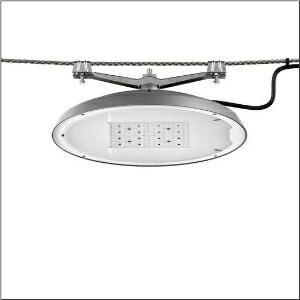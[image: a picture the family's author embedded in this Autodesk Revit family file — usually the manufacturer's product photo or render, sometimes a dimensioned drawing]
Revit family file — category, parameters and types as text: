
# Revit family: dl_r__50_iq_mini___st0_8s_5xa248v31f08me_3f47
name_source: partatom
category: Lighting Fixtures
units: mm (PartAtom-declared; Revit-internal decimal feet)

## family parameters
Cut with Voids When Loaded = No
Host = Face
Light Source = No
Part Type = Normal
Room Calculation Point = No
Round Connector Dimension = Use Diameter
Shared = No

## types (1)
- --- (1 x LED, 15660 lm, 107.8 W, 3000K)
    Apparent Load = 108 VA
    CIE Flux Codes = 38 75 97 100 100
    Color Rendering = 70
    Color Temperature = 3000K
    Default Elevation = 1800 mm
    Description = DL® 50 iQ mini, catenary luminaire, primary light control with lens, of PMMA, primary optical cover: cover, of toughened safety glass, transparent, light distribution: ST0.8s, light emission: direct distribution, primary light characteristic: symmetric, installation type: suspended mounting, LED, High Power LED, rated luminous flux: 15.660lm, luminous efficacy: 145lm/W, light colour: 730, colour temperature: 3000K, control gear: iQ Street-Remote, control: optimised constant luminous flux control (CLO 2.0), Desk-Remote (wireless, voltage-free reading and setting of iQ features in the workshop via application-optimized NFC function/RFID function), Light-Fading, Smart-Wire, Night-Set, Lumen-Switch, Temp-Guard, Auto-Match, Street-Remote, mains connection: 230..240V, AC, 50/60Hz, start of lifetime: 108W, end of service life: 118W, reduction: 47W, luminaire housing, of diecast aluminium, powder-coated, Siteco® metallic grey (DB 702S), diameter: 500mm, height: 115mm, mounting height: 4..12m, protection rating (complete): IP66, insulation class (complete): insulation class II (safety insulation), certification: CE, ENEC, ENEC+, VDE, impact resistance: IK08, permissible operating ambient temperature for outdoor applications: -25..+40°C, standard-compliant lighting for roads and squares, packaging unit: 1 piece

Light Distribution: ST0.8s
    Height = 124 mm  [stored 0.406824 ft]
    Lamp = 1 x LED
    Lamp Light Flux = 15660 lm
    Lamp Power = 107.8 W
    Lamp count = 1
    Length = 500 mm
    Luminous efficacy = 145 lm/W
    Manufacturer = Siteco
    ModVariant = No
    Model = 5XA248V31F08ME
    Number of Poles = 1
    OnlyDefault = Yes
    Power Factor = 1
    Product Name = DL® 50 iQ mini | ST0.8s
    Product group = catenary luminaire
    ProductGroupID = 6300
    Protection Class = Protection class II
    Protection Degree = IP 66
    RLX_Detail_Level = 1
    RLX_Emergency_Light_Flux = 0 lm
    RLX_Emergency_Type = 0
    RLX_Emergency_Type_DB = No
    RlxData = <blob elided: 127053 chars, md5=6730b871>
    Socket = socket
    Standby Power = 0 W
    System Light Flux = 15660 lm
    System Power = 108 W
    Type Comments = factory setting: luminous flux: 100 % | dim-lin: 254 | 565 mA
    Type Image = l_1251783.jpg
    URL = http://relux.com
    VarID = @adj_162461
    Voltage = 0 V
    Weight = 0.00 kg
    Width = 0 mm  [stored 0 ft]

note: [stored X ft] marks values corroborated as IEEE doubles in the binary element streams (Revit-internal decimal feet)

## geometry (parser evidence)
native form markers: Blend x4, Sweep x15
no freeform markers — native parametric forms only
